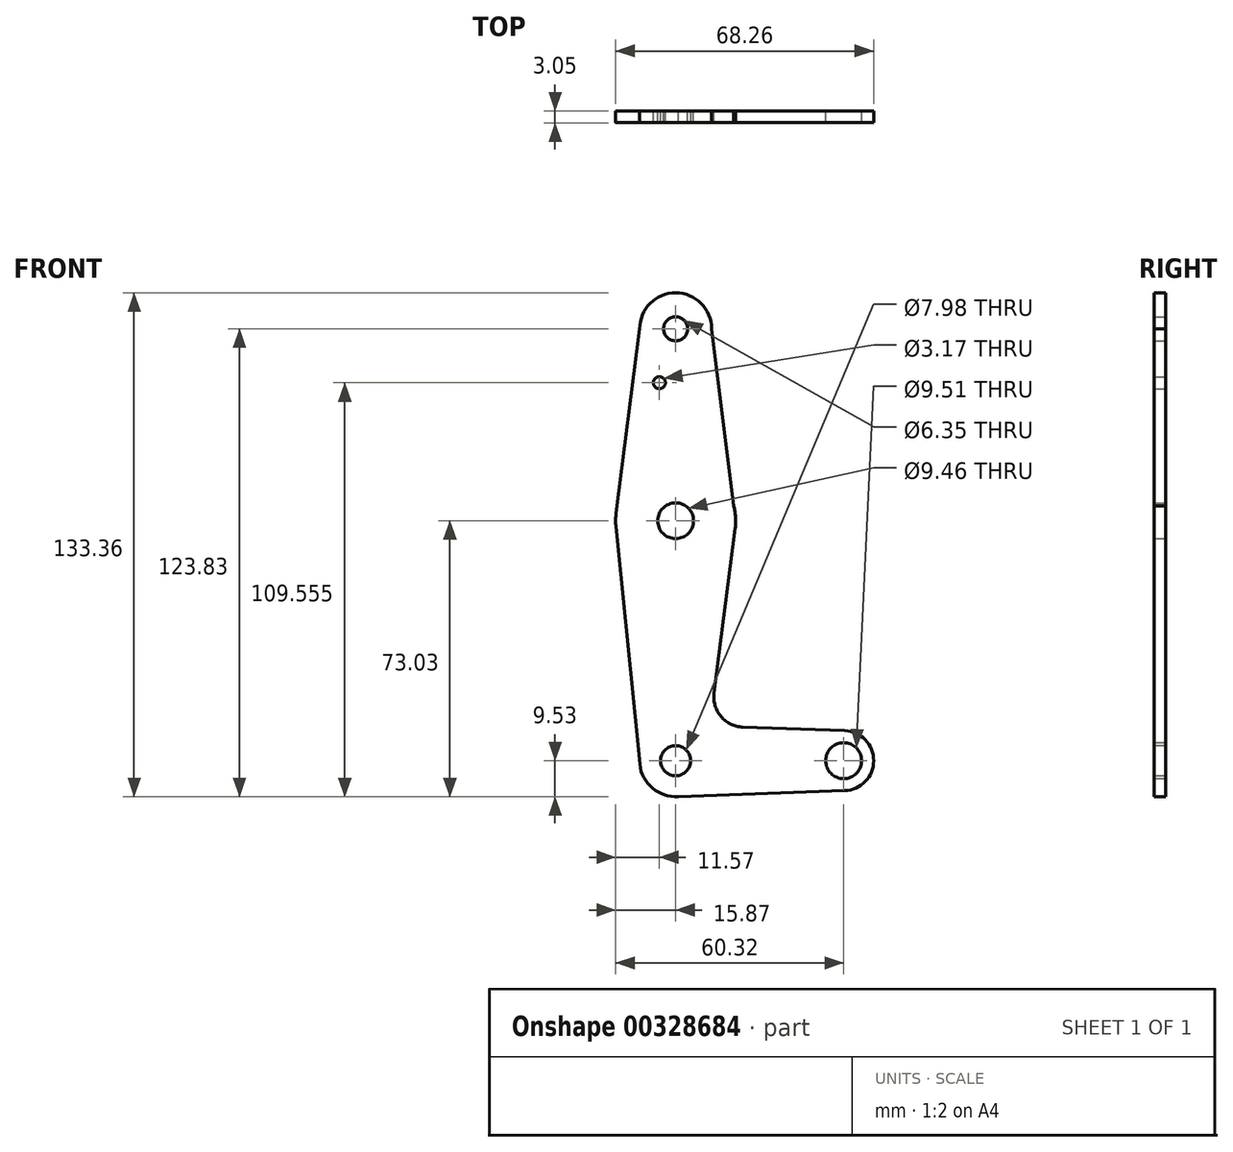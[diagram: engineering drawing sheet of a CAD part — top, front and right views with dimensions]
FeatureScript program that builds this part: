
annotation { "Feature Type Name" : "Feature", "Feature Type Description" : "" }
export const myFeature = defineFeature(function(context is Context, id is Id, definition is map)
    precondition{}
    {
        {
            var Q0;
            Q0=qCreatedBy(makeId("Front.planeOp"),FACE);
            var sketch = newSketch(context, id + "F0", { "sketchPlane" : qUnion([Q0])});
            skLineSegment(sketch, "E0", {"start": v(0, 0) * mm, "end": v(0, 114.3) * mm, "construction": true});
            skLineSegment(sketch, "E1", {"start": v(0, 0) * mm, "end": v(44.45, 0) * mm, "construction": true});
            skCircle(sketch, "E2", {"center": v(0, 114.3) * mm, "radius": 9.53 * mm});
            skCircle(sketch, "E3", {"center": v(44.45, 0) * mm, "radius": 7.94 * mm});
            skCircle(sketch, "E4", {"center": v(0, 0) * mm, "radius": 9.53 * mm});
            skCircle(sketch, "E5", {"center": v(0, 63.5) * mm, "radius": 15.88 * mm});
            skLineSegment(sketch, "E6", {"start": v(17.78, 8.9) * mm, "end": v(44.73, 7.93) * mm});
            skLineSegment(sketch, "E7", {"start": v(0, -9.53) * mm, "end": v(44.73, -7.93) * mm});
            skLineSegment(sketch, "E8", {"start": v(9.52, 114.3) * mm, "end": v(15.88, 63.5) * mm});
            skLineSegment(sketch, "E9", {"start": v(-9.53, 114.3) * mm, "end": v(-16, 63.5) * mm});
            skLineSegment(sketch, "E10", {"start": v(-15.8, 61.91) * mm, "end": v(-9.48, -0.95) * mm});
            skLineSegment(sketch, "E11", {"start": v(15.75, 61.5) * mm, "end": v(10.18, 17.84) * mm});
            skCircle(sketch, "E12", {"center": v(0, 63.5) * mm, "radius": 4.73 * mm});
            skCircle(sketch, "E13", {"center": v(0, 0) * mm, "radius": 3.99 * mm});
            skCircle(sketch, "E14", {"center": v(44.45, 0) * mm, "radius": 4.75 * mm});
            skPoint(sketch, "E15.newPointA", {"position": v(0, 9.53) * mm});
            skArc(sketch, "E15.filletArc", {"start": v(10.18, 17.84) * mm, "mid": v(12, 11.69) * mm, "end": v(17.78, 8.9) * mm});
            skCircle(sketch, "E16", {"center": v(-4.3, 100.03) * mm, "radius": 1.59 * mm});
            skCircle(sketch, "E17", {"center": v(0, 114.3) * mm, "radius": 3.18 * mm});
            skSolve(sketch);
        }
        {
            var Q0;
            Q0 = qSketchRegion(id + "F0", true);
            extrude(context, id + "F1", {"entities" : qUnion([Q0]), "depth" : 3.05 * mm});
        }
    });
